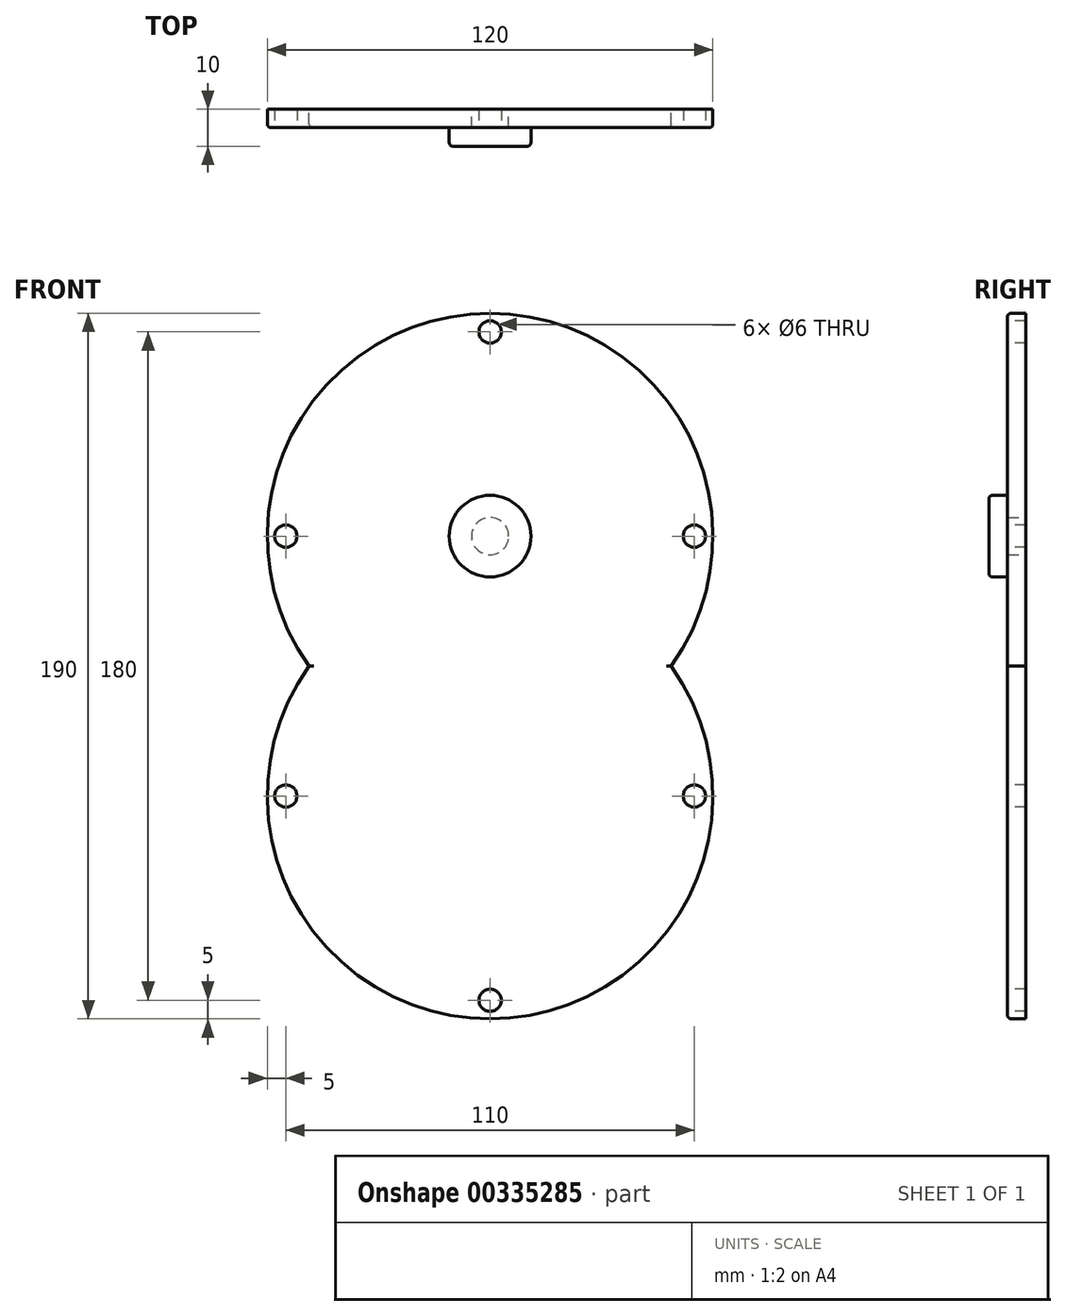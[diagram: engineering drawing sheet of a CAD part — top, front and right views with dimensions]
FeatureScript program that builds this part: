
annotation { "Feature Type Name" : "Feature", "Feature Type Description" : "" }
export const myFeature = defineFeature(function(context is Context, id is Id, definition is map)
    precondition{}
    {
        {
            var Q0;
            Q0=qCreatedBy(makeId("Front.planeOp"),FACE);
            var sketch = newSketch(context, id + "F0", { "sketchPlane" : qUnion([Q0])});
            skCircle(sketch, "E0", {"center": v(0, 35) * mm, "radius": 60 * mm});
            skCircle(sketch, "E1", {"center": v(0, -35) * mm, "radius": 60 * mm});
            skSolve(sketch);
        }
        {
            var Q0;
            {var subQ0=sQuery(id+"F0.wireOp",EDGE,"E1");var subQ1=sQuery(id+"F0.wireOp",EDGE,"E0");var subQ2=makeQuery(id+"F0.imprint","INTERSECT",VERTEX,{"disambiguationData":[OD(0.0)],"derivedFrom":[subQ1,subQ0]});Q0=makeQuery(id+"F0.imprint","IMPRINT",FACE,{"disambiguationData":[TD([[makeQuery(id+"F0.imprint","IMPRINT",EDGE,{"disambiguationData":[TD([[subQ2,1.0]])],"derivedFrom":subQ1}),1.0]])]});}
            var Q1;
            {var subQ0=sQuery(id+"F0.wireOp",EDGE,"E1");var subQ1=sQuery(id+"F0.wireOp",EDGE,"E0");var subQ2=makeQuery(id+"F0.imprint","INTERSECT",VERTEX,{"disambiguationData":[OD(0.0)],"derivedFrom":[subQ1,subQ0]});Q1=makeQuery(id+"F0.imprint","IMPRINT",FACE,{"disambiguationData":[TD([[makeQuery(id+"F0.imprint","IMPRINT",EDGE,{"disambiguationData":[TD([[subQ2,-1.0]])],"derivedFrom":subQ1}),1.0]])]});}
            var Q2;
            {var subQ0=sQuery(id+"F0.wireOp",EDGE,"E1");var subQ1=sQuery(id+"F0.wireOp",EDGE,"E0");var subQ2=makeQuery(id+"F0.imprint","INTERSECT",VERTEX,{"disambiguationData":[OD(0.0)],"derivedFrom":[subQ1,subQ0]});Q2=makeQuery(id+"F0.imprint","IMPRINT",FACE,{"disambiguationData":[TD([[makeQuery(id+"F0.imprint","IMPRINT",EDGE,{"disambiguationData":[TD([[subQ2,-1.0]])],"derivedFrom":subQ1}),-1.0]])]});}
            extrude(context, id + "F1", {"entities" : qUnion([Q0, Q1, Q2]), "depth" : 5 * mm});
        }
        {
            var Q0;
            Q0=makeQuery(id+"F1.opExtrude","CAP_FACE",FACE,{"disambiguationData":[OSD([sQuery(id+"F0.wireOp",EDGE,"E0"),sQuery(id+"F0.wireOp",EDGE,"E1")])],"isStart":false});
            var sketch = newSketch(context, id + "F2", { "sketchPlane" : qUnion([Q0])});
            skCircle(sketch, "E2", {"center": v(0, 35) * mm, "radius": 11 * mm});
            skSolve(sketch);
        }
        {
            var Q0;
            Q0=makeQuery(id+"F2.imprint","IMPRINT",FACE,{"disambiguationData":[TD([[makeQuery(id+"F2.imprint","IMPRINT",EDGE,{"derivedFrom":sQuery(id+"F2.wireOp",EDGE,"E2")}),1.0]])]});
            extrude(context, id + "F3", {"entities" : qUnion([Q0]), "operationType" : NewBodyOperationType.ADD, "depth" : 5 * mm});
        }
        {
            var Q0;
            Q0=makeQuery(id+"F1.opExtrude","CAP_FACE",FACE,{"disambiguationData":[OSD([sQuery(id+"F0.wireOp",EDGE,"E0"),sQuery(id+"F0.wireOp",EDGE,"E1")])],"isStart":true});
            var sketch = newSketch(context, id + "F4", { "sketchPlane" : qUnion([Q0])});
            skCircle(sketch, "E3", {"center": v(0, 35) * mm, "radius": 5 * mm});
            skSolve(sketch);
        }
        {
            var Q0;
            Q0=makeQuery(id+"F4.imprint","IMPRINT",FACE,{"disambiguationData":[TD([[makeQuery(id+"F4.imprint","IMPRINT",EDGE,{"derivedFrom":sQuery(id+"F4.wireOp",EDGE,"E3")}),1.0]])]});
            extrude(context, id + "F5", {"entities" : qUnion([Q0]), "operationType" : NewBodyOperationType.REMOVE, "oppositeDirection" : true, "depth" : 5 * mm});
        }
        {
            var Q0;
            Q0=makeQuery(id+"F3.opExtrude","CAP_EDGE",EDGE,{"disambiguationData":[OSD([sQuery(id+"F2.wireOp",EDGE,"E2")])],"isStart":false});
            var Q1;
            Q1=makeQuery(id+"F3.opExtrude","CAP_EDGE",EDGE,{"disambiguationData":[OSD([sQuery(id+"F2.wireOp",EDGE,"E2")])],"isStart":true});
            var Q2;
            Q2=makeQuery(id+"F1.opExtrude","CAP_EDGE",EDGE,{"disambiguationData":[OSD([sQuery(id+"F0.wireOp",EDGE,"E0")])],"isStart":false});
            var Q3;
            Q3=makeQuery(id+"F1.opExtrude","CAP_EDGE",EDGE,{"disambiguationData":[OSD([sQuery(id+"F0.wireOp",EDGE,"E1")])],"isStart":false});
            fillet(context, id + "F6", {"entities" : qUnion([Q0, Q1, Q2, Q3]), "radius" : 1 * mm, "tangentPropagation" : true, "allowEdgeOverflow" : false});
        }
        {
            var Q0;
            Q0=makeQuery(id+"F1.opExtrude","CAP_FACE",FACE,{"disambiguationData":[OSD([sQuery(id+"F0.wireOp",EDGE,"E0"),sQuery(id+"F0.wireOp",EDGE,"E1")])],"isStart":false});
            var sketch = newSketch(context, id + "F7", { "sketchPlane" : qUnion([Q0])});
            skCircle(sketch, "E4.0", {"center": v(0, 35) * mm, "radius": 12 * mm});
            skPoint(sketch, "E5", {"position": v(-55, 35) * mm});
            skPoint(sketch, "E6.1.0", {"position": v(0, 90) * mm});
            skPoint(sketch, "E6.2.0", {"position": v(55, 35) * mm});
            skLineSegment(sketch, "E6.anchor1", {"start": v(0, 35) * mm, "end": v(-55, 35) * mm, "construction": true});
            skLineSegment(sketch, "E6.anchor2", {"start": v(0, 35) * mm, "end": v(55, 35) * mm, "construction": true});
            skLineSegment(sketch, "E7", {"start": v(-47.5, 0) * mm, "end": v(47.5, 0) * mm, "construction": true});
            skPoint(sketch, "E8.MirrorP", {"position": v(-55, -35) * mm});
            skPoint(sketch, "E9.MirrorP", {"position": v(0, -90) * mm});
            skPoint(sketch, "E10.MirrorP", {"position": v(55, -35) * mm});
            skSolve(sketch);
        }
        {
            var Q0;
            Q0=sQuery(id+"F7.wireOp",VERTEX,"E6.1.0");
            var Q1;
            Q1=sQuery(id+"F7.wireOp",VERTEX,"E5");
            var Q2;
            Q2=sQuery(id+"F7.wireOp",VERTEX,"E8.MirrorP");
            var Q3;
            Q3=sQuery(id+"F7.wireOp",VERTEX,"E9.MirrorP");
            var Q4;
            Q4=sQuery(id+"F7.wireOp",VERTEX,"E10.MirrorP");
            var Q5;
            Q5=sQuery(id+"F7.wireOp",VERTEX,"E6.2.0");
            var Q6;
            Q6=makeQuery(id+"F1.opExtrude","SWEPT_BODY",BODY,{"disambiguationData":[OSD([sQuery(id+"F0.wireOp",EDGE,"E0"),sQuery(id+"F0.wireOp",EDGE,"E1")])]});
            hole(context, id + "F8", {"style" : HoleStyle.SIMPLE, "endStyle" : HoleEndStyle.BLIND, "holeDiameter" : 6 * mm, "holeDepth" : 20 * mm, "tappedDepth" : 12 * mm, "tapClearance" : 3, "startFromSketch" : true, "locations" : qUnion([Q0, Q1, Q2, Q3, Q4, Q5]), "scope" : qUnion([Q6])});
        }
    });
